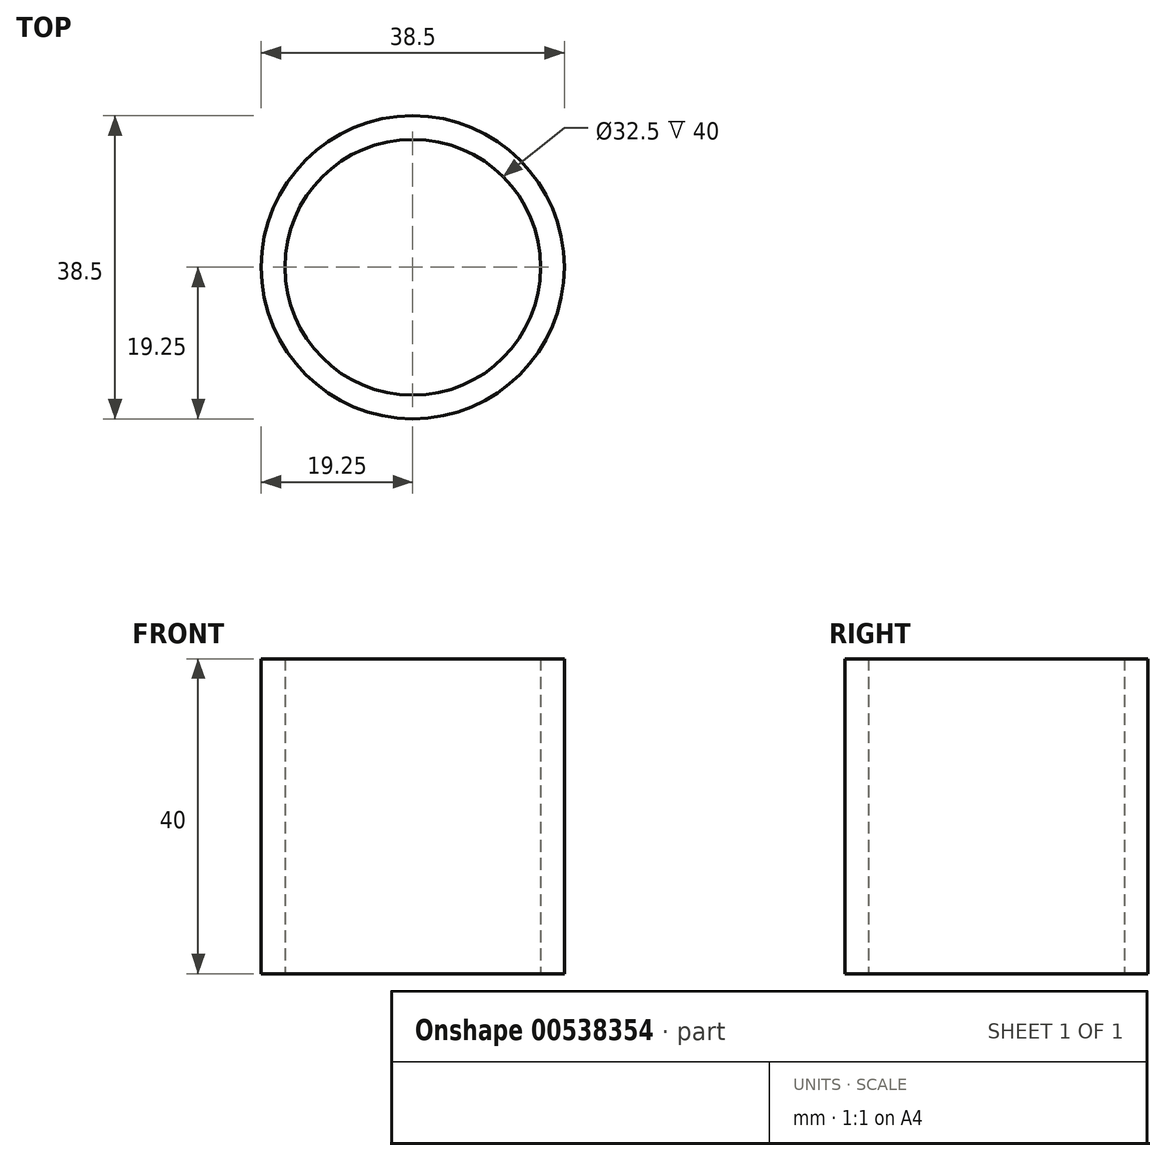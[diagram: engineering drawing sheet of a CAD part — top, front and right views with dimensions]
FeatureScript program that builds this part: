
annotation { "Feature Type Name" : "Feature", "Feature Type Description" : "" }
export const myFeature = defineFeature(function(context is Context, id is Id, definition is map)
    precondition{}
    {
        {
            var Q0;
            Q0=qCreatedBy(makeId("Top.planeOp"),FACE);
            var sketch = newSketch(context, id + "F0", { "sketchPlane" : qUnion([Q0])});
            skCircle(sketch, "E0", {"center": v(0, 0) * mm, "radius": 16.25 * mm});
            skCircle(sketch, "E1", {"center": v(0, 0) * mm, "radius": 19.25 * mm});
            skSolve(sketch);
        }
        {
            var Q0;
            Q0 = qSketchRegion(id + "F0", true);
            extrude(context, id + "F1", {"entities" : qUnion([Q0]), "depth" : 40 * mm, "offsetDistance" : 25 * mm});
        }
    });
